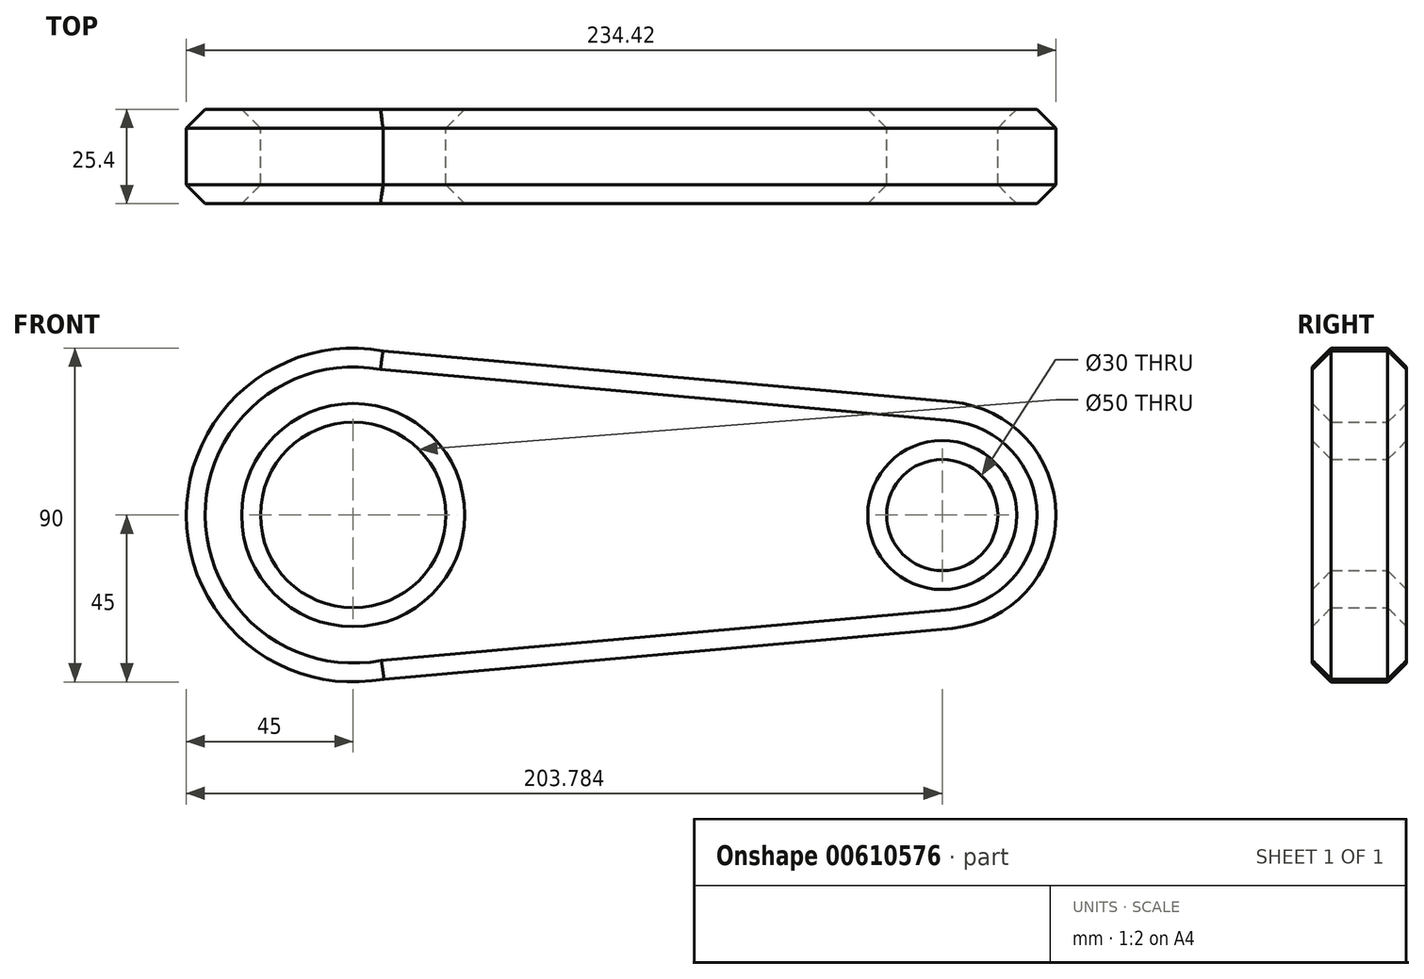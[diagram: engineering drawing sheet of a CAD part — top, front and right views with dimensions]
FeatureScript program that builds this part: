
annotation { "Feature Type Name" : "Feature", "Feature Type Description" : "" }
export const myFeature = defineFeature(function(context is Context, id is Id, definition is map)
    precondition{}
    {
        {
            var Q0;
            Q0=qCreatedBy(makeId("Front.planeOp"),FACE);
            var sketch = newSketch(context, id + "F0", { "sketchPlane" : qUnion([Q0])});
            skCircle(sketch, "E0", {"center": v(0, 0) * mm, "radius": 45 * mm});
            skCircle(sketch, "E1", {"center": v(0, 0) * mm, "radius": 25 * mm});
            skCircle(sketch, "E2", {"center": v(158.78, 0) * mm, "radius": 30.63 * mm});
            skCircle(sketch, "E3", {"center": v(158.78, 0) * mm, "radius": 15 * mm});
            skLineSegment(sketch, "E4", {"start": v(0, 45) * mm, "end": v(161.52, 30.5) * mm});
            skLineSegment(sketch, "E5", {"start": v(-0.3, -45) * mm, "end": v(161.52, -30.5) * mm});
            skSolve(sketch);
        }
        {
            var Q0;
            Q0 = qSketchRegion(id + "F0", true);
            extrude(context, id + "F1", {"entities" : qUnion([Q0]), "depth" : 25.4 * mm, "offsetDistance" : 25.4 * mm});
        }
        {
            var Q0;
            Q0=makeQuery(id+"F1.opExtrude","CAP_EDGE",EDGE,{"disambiguationData":[OSD([sQuery(id+"F0.wireOp",EDGE,"E4")])],"isStart":false});
            var Q1;
            Q1=makeQuery(id+"F1.opExtrude","CAP_EDGE",EDGE,{"disambiguationData":[OSD([sQuery(id+"F0.wireOp",EDGE,"E4")])],"isStart":true});
            var Q2;
            Q2=makeQuery(id+"F1.opExtrude","CAP_EDGE",EDGE,{"disambiguationData":[OSD([sQuery(id+"F0.wireOp",EDGE,"E0")])],"isStart":false});
            var Q3;
            Q3=makeQuery(id+"F1.opExtrude","CAP_EDGE",EDGE,{"disambiguationData":[OSD([sQuery(id+"F0.wireOp",EDGE,"E0")])],"isStart":true});
            var Q4;
            Q4=makeQuery(id+"F1.opExtrude","CAP_EDGE",EDGE,{"disambiguationData":[OSD([sQuery(id+"F0.wireOp",EDGE,"E3")])],"isStart":false});
            var Q5;
            Q5=makeQuery(id+"F1.opExtrude","CAP_EDGE",EDGE,{"disambiguationData":[OSD([sQuery(id+"F0.wireOp",EDGE,"E3")])],"isStart":true});
            var Q6;
            Q6=makeQuery(id+"F1.opExtrude","SWEPT_FACE",FACE,{"disambiguationData":[OSD([sQuery(id+"F0.wireOp",EDGE,"E1")])]});
            chamfer(context, id + "F2", {"entities" : qUnion([Q0, Q1, Q2, Q3, Q4, Q5, Q6]), "width" : 5.08 * mm, "tangentPropagation" : true});
        }
    });
